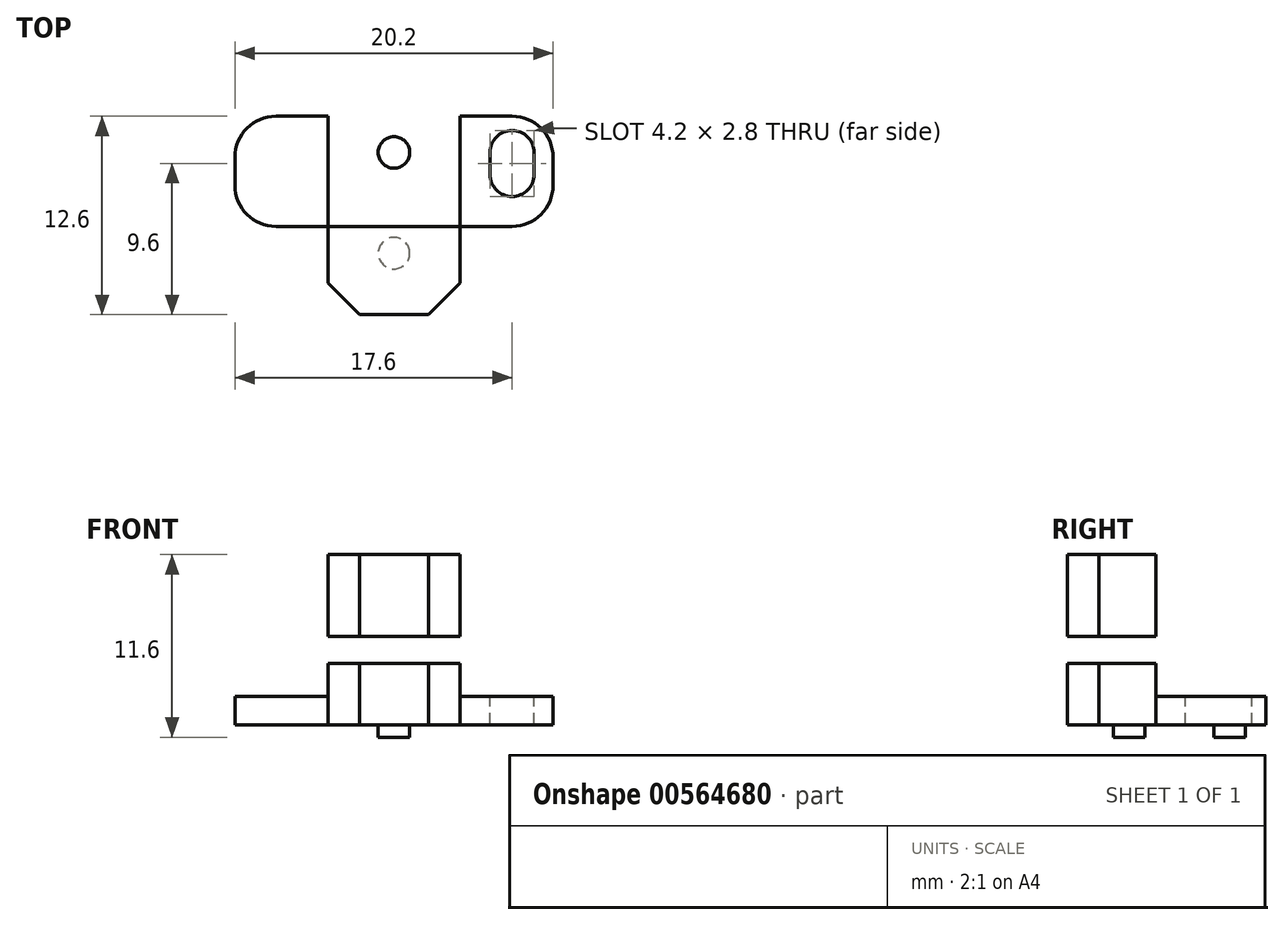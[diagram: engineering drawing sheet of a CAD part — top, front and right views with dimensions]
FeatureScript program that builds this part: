
annotation { "Feature Type Name" : "Feature", "Feature Type Description" : "" }
export const myFeature = defineFeature(function(context is Context, id is Id, definition is map)
    precondition{}
    {
        {
            var Q0;
            Q0=qCreatedBy(makeId("Top.planeOp"),FACE);
            var sketch = newSketch(context, id + "F0", { "sketchPlane" : qUnion([Q0])});
            skLineSegment(sketch, "E0.bottom", {"start": v(-10.1, 0) * mm, "end": v(10.1, 0) * mm});
            skLineSegment(sketch, "E0.top", {"start": v(-10.1, -7) * mm, "end": v(10.1, -7) * mm});
            skLineSegment(sketch, "E0.left", {"start": v(-10.1, 0) * mm, "end": v(-10.1, -7) * mm});
            skLineSegment(sketch, "E0.right", {"start": v(10.1, 0) * mm, "end": v(10.1, -7) * mm});
            skLineSegment(sketch, "E1.bottom", {"start": v(-4.2, 0) * mm, "end": v(4.2, 0) * mm});
            skLineSegment(sketch, "E1.top", {"start": v(-4.2, -12.6) * mm, "end": v(4.2, -12.6) * mm});
            skLineSegment(sketch, "E1.left", {"start": v(-4.2, 0) * mm, "end": v(-4.2, -12.6) * mm});
            skLineSegment(sketch, "E1.right", {"start": v(4.2, 0) * mm, "end": v(4.2, -12.6) * mm});
            skSolve(sketch);
        }
        {
            var Q0;
            {var subQ0=sQuery(id+"F0.wireOp",EDGE,"E0.left");Q0=makeQuery(id+"F0.imprint","IMPRINT",FACE,{"disambiguationData":[TD([[makeQuery(id+"F0.imprint","IMPRINT",EDGE,{"derivedFrom":subQ0}),1.0]])]});}
            var Q1;
            {var subQ5=sQuery(id+"F0.wireOp",EDGE,"E1.bottom");Q1=makeQuery(id+"F0.imprint","IMPRINT",FACE,{"disambiguationData":[TD([[makeQuery(id+"F0.imprint","IMPRINT",EDGE,{"derivedFrom":subQ5}),-1.0]])]});}
            var Q2;
            {var subQ0=sQuery(id+"F0.wireOp",EDGE,"E0.right");Q2=makeQuery(id+"F0.imprint","IMPRINT",FACE,{"disambiguationData":[TD([[makeQuery(id+"F0.imprint","IMPRINT",EDGE,{"derivedFrom":subQ0}),-1.0]])]});}
            extrude(context, id + "F1", {"entities" : qUnion([Q0, Q1, Q2]), "depth" : 1.8 * mm, "offsetDistance" : 25.4 * mm});
        }
        {
            var Q0;
            {var subQ5=sQuery(id+"F0.wireOp",EDGE,"E1.top");Q0=makeQuery(id+"F0.imprint","IMPRINT",FACE,{"disambiguationData":[TD([[makeQuery(id+"F0.imprint","IMPRINT",EDGE,{"derivedFrom":subQ5}),1.0]])]});}
            var Q1;
            {var subQ5=sQuery(id+"F0.wireOp",EDGE,"E1.bottom");Q1=makeQuery(id+"F0.imprint","IMPRINT",FACE,{"disambiguationData":[TD([[makeQuery(id+"F0.imprint","IMPRINT",EDGE,{"derivedFrom":subQ5}),-1.0]])]});}
            extrude(context, id + "F2", {"entities" : qUnion([Q0, Q1]), "operationType" : NewBodyOperationType.ADD, "depth" : 10.8 * mm, "offsetDistance" : 25.4 * mm});
        }
        {
            var Q0;
            {var subQ0=sQuery(id+"F0.wireOp",EDGE,"E1.left");var subQ1=sQuery(id+"F0.wireOp",EDGE,"E1.top");Q0=makeQuery(id+"F9.boolean.opBoolean","SPLIT",EDGE,{"disambiguationData":[TD([makeQuery(id+"F9.opExtrude","SWEPT_FACE",FACE,{"disambiguationData":[OSD([sQuery(id+"F8.wireOp",EDGE,"E8.top")])]})])],"derivedFrom":makeQuery(id+"F2.opExtrude","SWEPT_EDGE",EDGE,{"disambiguationData":[OSD([subQ1,subQ0])]})});}
            var Q1;
            {var subQ0=sQuery(id+"F0.wireOp",EDGE,"E1.right");var subQ1=sQuery(id+"F0.wireOp",EDGE,"E1.top");Q1=makeQuery(id+"F9.boolean.opBoolean","SPLIT",EDGE,{"disambiguationData":[TD([makeQuery(id+"F9.opExtrude","SWEPT_FACE",FACE,{"disambiguationData":[OSD([sQuery(id+"F8.wireOp",EDGE,"E8.top")])]})])],"derivedFrom":makeQuery(id+"F2.opExtrude","SWEPT_EDGE",EDGE,{"disambiguationData":[OSD([subQ1,subQ0])]})});}
            chamfer(context, id + "F3", {"entities" : qUnion([Q0, Q1]), "width" : 2 * mm, "tangentPropagation" : true});
        }
        {
            var Q0;
            {var subQ0=sQuery(id+"F0.wireOp",EDGE,"E1.bottom");Q0=makeQuery(id+"F2.boolean.opBoolean","MERGE",FACE,{"derivedFrom":[makeQuery(id+"F1.opExtrude","CAP_FACE",FACE,{"disambiguationData":[OSD([sQuery(id+"F0.wireOp",EDGE,"E0.bottom"),sQuery(id+"F0.wireOp",EDGE,"E0.top"),sQuery(id+"F0.wireOp",EDGE,"E0.left"),sQuery(id+"F0.wireOp",EDGE,"E0.right"),subQ0])],"isStart":true}),makeQuery(id+"F2.opExtrude","CAP_FACE",FACE,{"disambiguationData":[OSD([subQ0,sQuery(id+"F0.wireOp",EDGE,"E1.top"),sQuery(id+"F0.wireOp",EDGE,"E1.left"),sQuery(id+"F0.wireOp",EDGE,"E1.right")])],"isStart":true})]});}
            var sketch = newSketch(context, id + "F4", { "sketchPlane" : qUnion([Q0])});
            skCircle(sketch, "E2", {"center": v(0, 2.3) * mm, "radius": 1 * mm});
            skCircle(sketch, "E3", {"center": v(0, 8.7) * mm, "radius": 1 * mm});
            skSolve(sketch);
        }
        {
            var Q0;
            Q0 = qSketchRegion(id + "F4", true);
            extrude(context, id + "F5", {"entities" : qUnion([Q0]), "operationType" : NewBodyOperationType.ADD, "depth" : .8 * mm, "offsetDistance" : 25.4 * mm});
        }
        {
            var Q0;
            {var subQ0=sQuery(id+"F0.wireOp",EDGE,"E1.bottom");var subQ1=sQuery(id+"F0.wireOp",EDGE,"E0.left");var subQ2=sQuery(id+"F0.wireOp",EDGE,"E0.top");var subQ3=sQuery(id+"F0.wireOp",EDGE,"E0.bottom");Q0=makeQuery(id+"F2.boolean.opBoolean","SPLIT",FACE,{"disambiguationData":[TD([makeQuery(id+"F1.opExtrude","SWEPT_FACE",FACE,{"disambiguationData":[OSD([subQ1])]})])],"derivedFrom":makeQuery(id+"F1.opExtrude","CAP_FACE",FACE,{"disambiguationData":[OSD([subQ3,subQ2,subQ1,sQuery(id+"F0.wireOp",EDGE,"E0.right"),subQ0])],"isStart":false})});}
            var sketch = newSketch(context, id + "F6", { "sketchPlane" : qUnion([Q0])});
            skArc(sketch, "E4", {"start": v(8.9, -2.3) * mm, "mid": v(7.5, -0.9) * mm, "end": v(6.1, -2.3) * mm});
            skArc(sketch, "E5", {"start": v(6.1, -3.7) * mm, "mid": v(7.5, -5.1) * mm, "end": v(8.9, -3.7) * mm});
            skLineSegment(sketch, "E6", {"start": v(6.1, -2.3) * mm, "end": v(6.1, -3.7) * mm});
            skLineSegment(sketch, "E7", {"start": v(8.9, -2.3) * mm, "end": v(8.9, -3.7) * mm});
            skSolve(sketch);
        }
        {
            var Q0;
            Q0=makeQuery(id+"F6.imprint","IMPRINT",FACE,{"disambiguationData":[TD([[makeQuery(id+"F6.imprint","IMPRINT",EDGE,{"derivedFrom":sQuery(id+"F6.wireOp",EDGE,"E4")}),1.0]])]});
            extrude(context, id + "F7", {"entities" : qUnion([Q0]), "operationType" : NewBodyOperationType.REMOVE, "endBound" : BoundingType.THROUGH_ALL, "oppositeDirection" : true, "depth" : 25.4 * mm, "offsetDistance" : 25.4 * mm});
        }
        {
            var Q0;
            Q0=makeQuery(id+"F2.opExtrude","SWEPT_FACE",FACE,{"disambiguationData":[OSD([sQuery(id+"F0.wireOp",EDGE,"E1.left")])]});
            var sketch = newSketch(context, id + "F8", { "sketchPlane" : qUnion([Q0])});
            skLineSegment(sketch, "E8.bottom", {"start": v(12.6, 3.9) * mm, "end": v(4.5, 3.9) * mm});
            skLineSegment(sketch, "E8.top", {"start": v(12.6, 5.6) * mm, "end": v(4.5, 5.6) * mm});
            skLineSegment(sketch, "E8.left", {"start": v(12.6, 3.9) * mm, "end": v(12.6, 5.6) * mm});
            skLineSegment(sketch, "E8.right", {"start": v(4.5, 3.9) * mm, "end": v(4.5, 5.6) * mm});
            skSolve(sketch);
        }
        {
            var Q0;
            Q0=makeQuery(id+"F8.imprint","IMPRINT",FACE,{"disambiguationData":[TD([[makeQuery(id+"F8.imprint","IMPRINT",EDGE,{"derivedFrom":sQuery(id+"F8.wireOp",EDGE,"E8.bottom")}),-1.0]])]});
            extrude(context, id + "F9", {"entities" : qUnion([Q0]), "operationType" : NewBodyOperationType.REMOVE, "endBound" : BoundingType.THROUGH_ALL, "oppositeDirection" : true, "depth" : 25 * mm, "offsetDistance" : 25 * mm});
        }
        {
            var Q0;
            Q0=makeQuery(id+"F1.opExtrude","SWEPT_EDGE",EDGE,{"disambiguationData":[OSD([sQuery(id+"F0.wireOp",EDGE,"E0.top"),sQuery(id+"F0.wireOp",EDGE,"E0.left")])]});
            var Q1;
            Q1=makeQuery(id+"F1.opExtrude","SWEPT_EDGE",EDGE,{"disambiguationData":[OSD([sQuery(id+"F0.wireOp",EDGE,"E0.bottom"),sQuery(id+"F0.wireOp",EDGE,"E0.left")])]});
            var Q2;
            Q2=makeQuery(id+"F1.opExtrude","SWEPT_EDGE",EDGE,{"disambiguationData":[OSD([sQuery(id+"F0.wireOp",EDGE,"E0.top"),sQuery(id+"F0.wireOp",EDGE,"E0.right")])]});
            var Q3;
            Q3=makeQuery(id+"F1.opExtrude","SWEPT_EDGE",EDGE,{"disambiguationData":[OSD([sQuery(id+"F0.wireOp",EDGE,"E0.bottom"),sQuery(id+"F0.wireOp",EDGE,"E0.right")])]});
            fillet(context, id + "F10", {"entities" : qUnion([Q0, Q1, Q2, Q3]), "radius" : 2.6 * mm, "tangentPropagation" : true, "allowEdgeOverflow" : false});
        }
        {
            var Q0;
            Q0=makeQuery(id+"F5.opExtrude","CAP_FACE",FACE,{"disambiguationData":[OSD([sQuery(id+"F4.wireOp",EDGE,"E3")])],"isStart":false});
            var sketch = newSketch(context, id + "F11", { "sketchPlane" : qUnion([Q0])});
            skPoint(sketch, "E9", {"position": v(0, 8.7) * mm});
            skSolve(sketch);
        }
        {
            var Q0;
            {var subQ2=sQuery(id+"F0.wireOp",EDGE,"E1.top");Q0=makeQuery(id+"F9.boolean.opBoolean","SPLIT",FACE,{"disambiguationData":[TD([makeQuery(id+"F9.opExtrude","SWEPT_FACE",FACE,{"disambiguationData":[OSD([sQuery(id+"F8.wireOp",EDGE,"E8.top")])]})])],"derivedFrom":makeQuery(id+"F2.opExtrude","SWEPT_FACE",FACE,{"disambiguationData":[OSD([subQ2])]})});}
            var Q1;
            Q1=sQuery(id+"F11.wireOp",VERTEX,"E9");
            cPlane(context, id + "F12", {"entities" : qUnion([Q0, Q1]), "cplaneType" : CPlaneType.PLANE_POINT, "offset" : 0.13 * mm, "oppositeDirection" : true, "width" : 152.4 * mm, "height" : 152.4 * mm});
        }
    });
